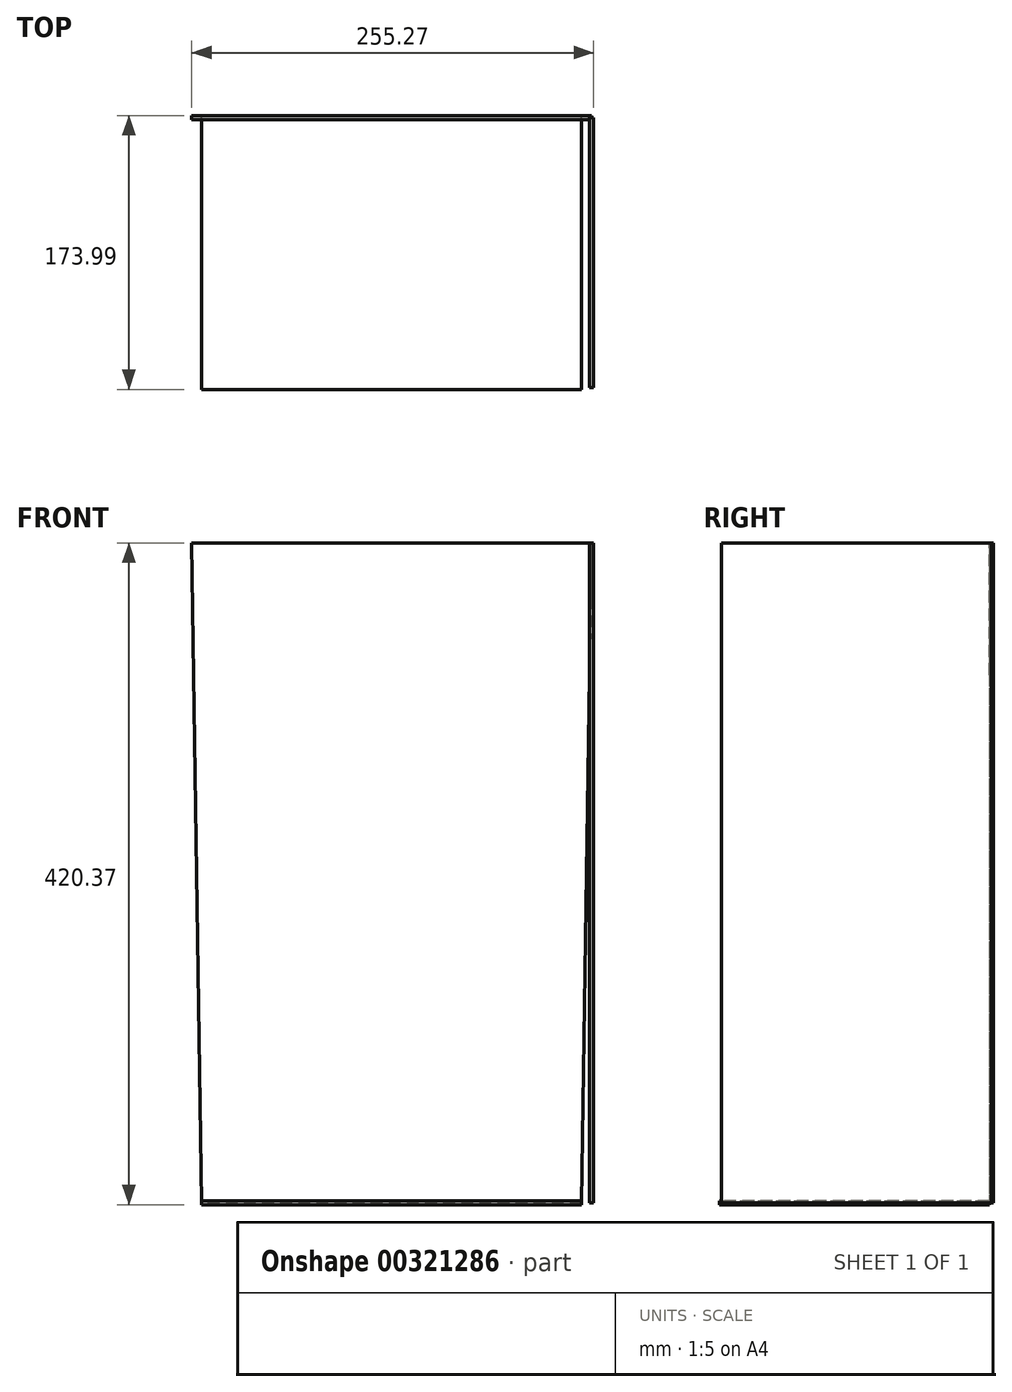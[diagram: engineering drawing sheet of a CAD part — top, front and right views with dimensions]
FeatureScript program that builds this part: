
annotation { "Feature Type Name" : "Feature", "Feature Type Description" : "" }
export const myFeature = defineFeature(function(context is Context, id is Id, definition is map)
    precondition{}
    {
        {
            var Q0;
            Q0=qCreatedBy(makeId("Front.planeOp"),FACE);
            var sketch = newSketch(context, id + "F0", { "sketchPlane" : qUnion([Q0])});
            skPoint(sketch, "E0.middle", {"position": v(0, 0) * mm});
            skLineSegment(sketch, "E1", {"start": v(0, 419.05) * mm, "end": v(-254, 419.05) * mm});
            skLineSegment(sketch, "E2", {"start": v(-6.35, 0) * mm, "end": v(-247.65, 0) * mm});
            skLineSegment(sketch, "E3", {"start": v(-254, 419.05) * mm, "end": v(-247.65, 0) * mm});
            skLineSegment(sketch, "E4", {"start": v(0, 419.05) * mm, "end": v(-6.35, 0) * mm});
            skLineSegment(sketch, "E5", {"start": v(-127, 419.05) * mm, "end": v(-127, 0) * mm, "construction": true});
            skSolve(sketch);
        }
        {
            var Q0;
            Q0=makeQuery(id+"F0.imprint","IMPRINT",FACE,{"disambiguationData":[TD([[makeQuery(id+"F0.imprint","IMPRINT",EDGE,{"derivedFrom":sQuery(id+"F0.wireOp",EDGE,"E1")}),1.0]])]});
            extrude(context, id + "F1", {"entities" : qUnion([Q0]), "endBound" : BoundingType.SYMMETRIC, "depth" : 2.54 * mm});
        }
        {
            var Q0;
            Q0=qCreatedBy(makeId("Top.planeOp"),FACE);
            var sketch = newSketch(context, id + "F2", { "sketchPlane" : qUnion([Q0])});
            skLineSegment(sketch, "E6", {"start": v(-247.65, -1.27) * mm, "end": v(-247.65, -172.72) * mm});
            skLineSegment(sketch, "E7", {"start": v(-247.65, -172.72) * mm, "end": v(-6.35, -172.72) * mm});
            skLineSegment(sketch, "E8", {"start": v(-6.35, -172.72) * mm, "end": v(-6.35, -1.27) * mm});
            skLineSegment(sketch, "E9", {"start": v(-6.35, -1.27) * mm, "end": v(-247.65, -1.27) * mm});
            skSolve(sketch);
        }
        {
            var Q0;
            Q0=makeQuery(id+"F2.imprint","IMPRINT",FACE,{"disambiguationData":[TD([[makeQuery(id+"F2.imprint","IMPRINT",EDGE,{"derivedFrom":sQuery(id+"F2.wireOp",EDGE,"E6")}),1.0]])]});
            extrude(context, id + "F3", {"entities" : qUnion([Q0]), "operationType" : NewBodyOperationType.ADD, "endBound" : BoundingType.SYMMETRIC, "depth" : 2.54 * mm});
        }
        {
            var Q0;
            Q0=qCreatedBy(makeId("Right.planeOp"),FACE);
            var sketch = newSketch(context, id + "F4", { "sketchPlane" : qUnion([Q0])});
            skLineSegment(sketch, "E10", {"start": v(0, 0) * mm, "end": v(-171.45, 0) * mm});
            skLineSegment(sketch, "E11", {"start": v(-171.45, 0) * mm, "end": v(-171.45, 419.1) * mm});
            skLineSegment(sketch, "E12", {"start": v(-171.45, 419.1) * mm, "end": v(0, 419.1) * mm});
            skLineSegment(sketch, "E13", {"start": v(0, 419.1) * mm, "end": v(0, 0) * mm});
            skSolve(sketch);
        }
        {
            var Q0;
            Q0 = qSketchRegion(id + "F4", true);
            extrude(context, id + "F5", {"entities" : qUnion([Q0]), "operationType" : NewBodyOperationType.ADD, "endBound" : BoundingType.SYMMETRIC, "depth" : 2.54 * mm});
        }
    });
